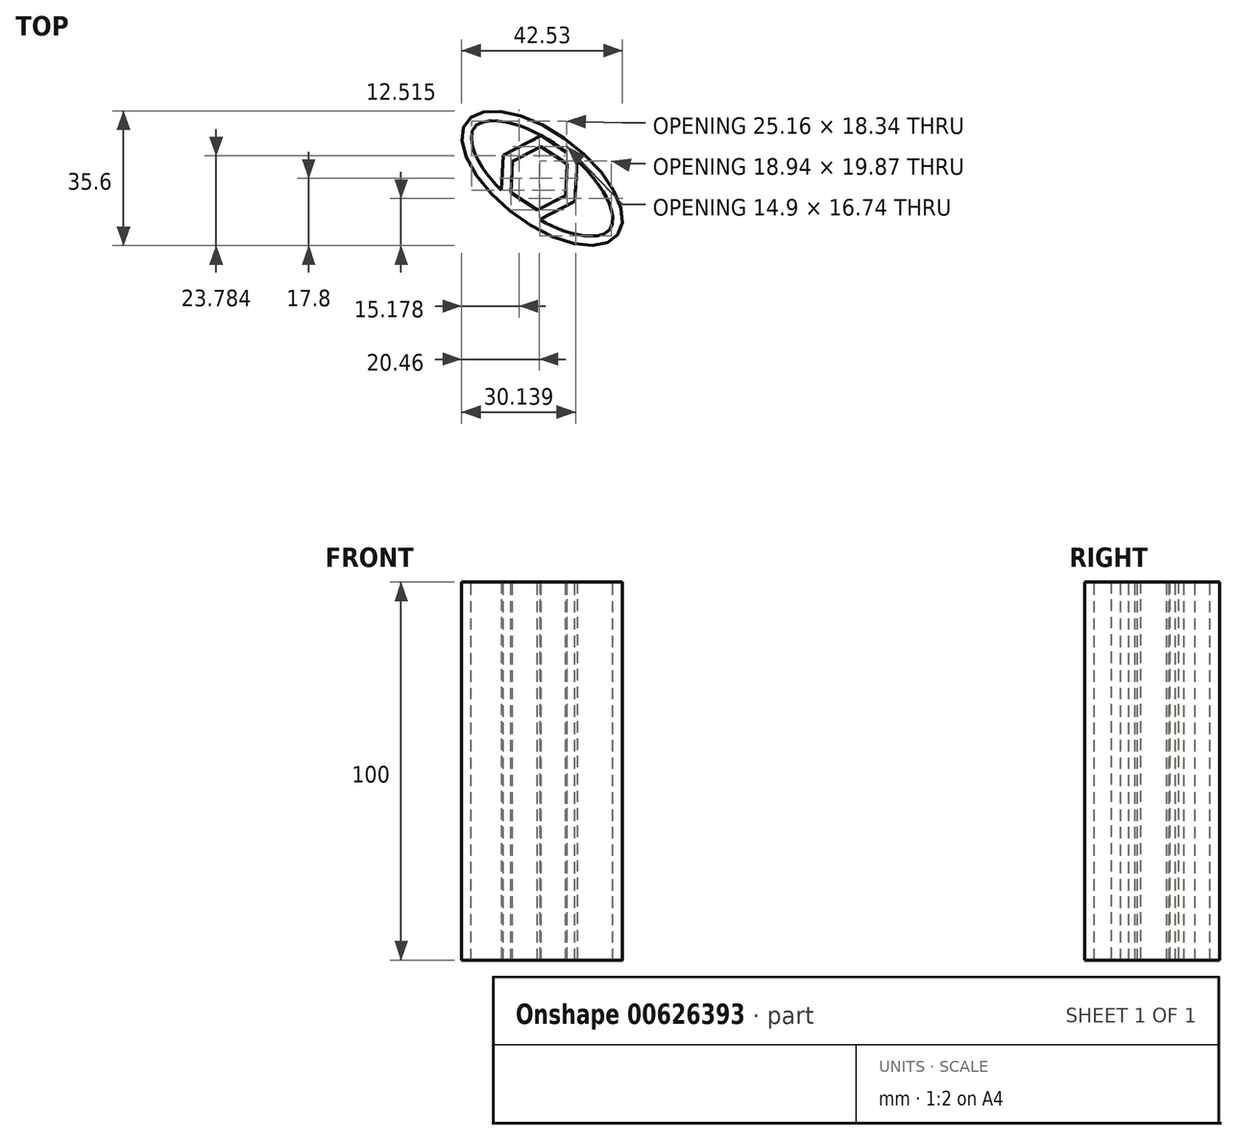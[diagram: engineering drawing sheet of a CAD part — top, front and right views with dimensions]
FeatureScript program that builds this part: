
annotation { "Feature Type Name" : "Feature", "Feature Type Description" : "" }
export const myFeature = defineFeature(function(context is Context, id is Id, definition is map)
    precondition{}
    {
        {
            var Q0;
            Q0=qCreatedBy(makeId("Top.planeOp"),FACE);
            var sketch = newSketch(context, id + "F0", { "sketchPlane" : qUnion([Q0])});
            skEllipse(sketch, "E0", {"center": v(0.8, 0) * mm, "majorRadius": 25 * mm, "minorRadius": 12 * mm, "majorAxis": v(0.8, -0.6)});
            skSolve(sketch);
        }
        {
            var Q0;
            Q0 = qSketchRegion(id + "F0", true);
            extrude(context, id + "F1", {"entities" : qUnion([Q0]), "endBound" : BoundingType.SYMMETRIC, "depth" : 100 * mm, "offsetDistance" : 25.4 * mm});
        }
        {
            var Q0;
            Q0=makeQuery(id+"F1.opExtrude","CAP_FACE",FACE,{"disambiguationData":[OSD([sQuery(id+"F0.wireOp",EDGE,"E0")])],"isStart":false});
            var sketch = newSketch(context, id + "F2", { "sketchPlane" : qUnion([Q0])});
            skCircle(sketch, "E1.cCircle", {"center": v(0, 0) * mm, "radius": 7.26 * mm, "construction": true});
            skLineSegment(sketch, "E1.0", {"start": v(7.05, -4.53) * mm, "end": v(-0.4, -8.37) * mm});
            skLineSegment(sketch, "E1.1", {"start": v(-0.4, -8.37) * mm, "end": v(-7.45, -3.84) * mm});
            skLineSegment(sketch, "E1.2", {"start": v(-7.45, -3.84) * mm, "end": v(-7.05, 4.53) * mm});
            skLineSegment(sketch, "E1.3", {"start": v(-7.05, 4.53) * mm, "end": v(0.4, 8.37) * mm});
            skLineSegment(sketch, "E1.4", {"start": v(0.4, 8.37) * mm, "end": v(7.45, 3.84) * mm});
            skLineSegment(sketch, "E1.5", {"start": v(7.45, 3.84) * mm, "end": v(7.05, -4.53) * mm});
            skPoint(sketch, "E1.0.midPoint", {"position": v(3.32, -6.45) * mm});
            skSolve(sketch);
        }
        {
            var Q0;
            Q0=makeQuery(id+"F2.imprint","IMPRINT",FACE,{"disambiguationData":[TD([[makeQuery(id+"F2.imprint","IMPRINT",EDGE,{"derivedFrom":sQuery(id+"F2.wireOp",EDGE,"E1.0")}),-1.0]])]});
            extrude(context, id + "F3", {"entities" : qUnion([Q0]), "operationType" : NewBodyOperationType.REMOVE, "endBound" : BoundingType.THROUGH_ALL, "oppositeDirection" : true, "depth" : 25.4 * mm, "offsetDistance" : 25.4 * mm});
        }
        {
            var Q0;
            Q0=makeQuery(id+"F1.opExtrude","CAP_FACE",FACE,{"disambiguationData":[OSD([sQuery(id+"F0.wireOp",EDGE,"E0")])],"isStart":false});
            var Q1;
            Q1=makeQuery(id+"F1.opExtrude","CAP_FACE",FACE,{"disambiguationData":[OSD([sQuery(id+"F0.wireOp",EDGE,"E0")])],"isStart":true});
            var Q2;
            Q2=makeQuery(id+"F1.opExtrude","SWEPT_BODY",BODY,{"disambiguationData":[OSD([sQuery(id+"F0.wireOp",EDGE,"E0")])]});
            shell(context, id + "F4", {"entities" : qUnion([Q0, Q1]), "parts" : qUnion([Q2]), "thickness" : 2.54 * mm});
        }
    });
